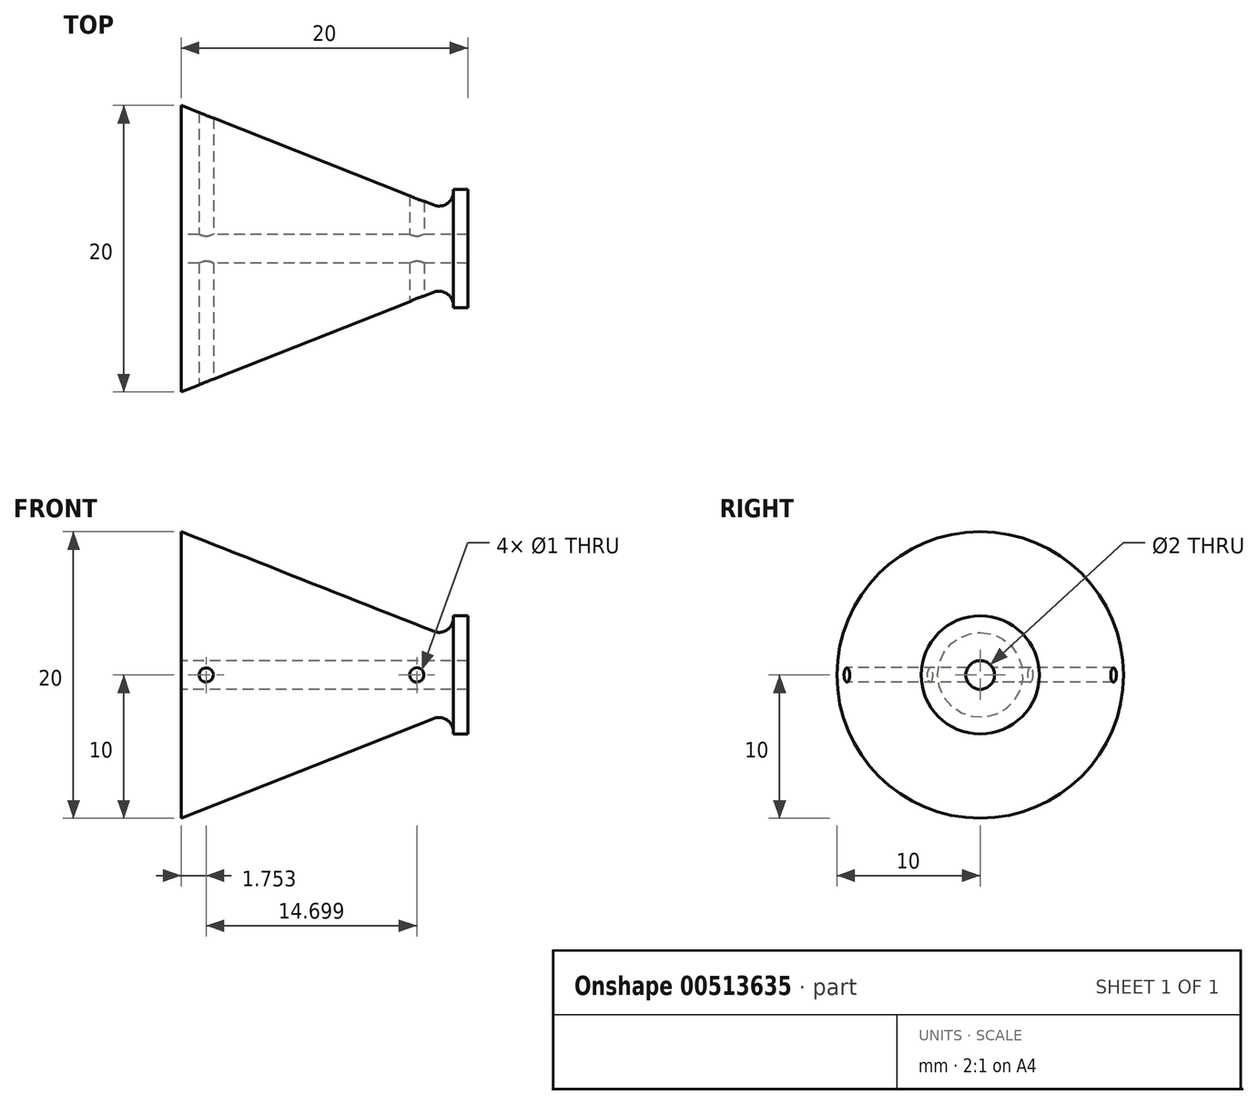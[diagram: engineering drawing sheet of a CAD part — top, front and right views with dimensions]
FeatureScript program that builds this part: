
annotation { "Feature Type Name" : "Feature", "Feature Type Description" : "" }
export const myFeature = defineFeature(function(context is Context, id is Id, definition is map)
    precondition{}
    {
        {
            var Q0;
            Q0=qCreatedBy(makeId("Front.planeOp"),FACE);
            var sketch = newSketch(context, id + "F0", { "sketchPlane" : qUnion([Q0])});
            skLineSegment(sketch, "E0", {"start": v(-20.44, 0) * mm, "end": v(36.79, 0) * mm, "construction": true});
            skLineSegment(sketch, "E1", {"start": v(0, 1) * mm, "end": v(0, 10) * mm});
            skLineSegment(sketch, "E2", {"start": v(0, 10) * mm, "end": v(19, 2.5) * mm});
            skLineSegment(sketch, "E3", {"start": v(19, 2.5) * mm, "end": v(19, 4.12) * mm});
            skLineSegment(sketch, "E4", {"start": v(19, 4.12) * mm, "end": v(20, 4.12) * mm});
            skLineSegment(sketch, "E5", {"start": v(20, 4.12) * mm, "end": v(20, 1) * mm});
            skLineSegment(sketch, "E6", {"start": v(0, 1) * mm, "end": v(20, 1) * mm});
            skSolve(sketch);
        }
        {
            var Q0;
            Q0=makeQuery(id+"F0.imprint","IMPRINT",FACE,{"disambiguationData":[TD([[makeQuery(id+"F0.imprint","IMPRINT",EDGE,{"derivedFrom":sQuery(id+"F0.wireOp",EDGE,"E1")}),-1.0]])]});
            var Q1;
            Q1=sQuery(id+"F0.wireOp",EDGE,"E0");
            revolve(context, id + "F1", {"entities" : qUnion([Q0]), "axis" : qUnion([Q1]), "revolveType" : RevolveType.FULL});
        }
        {
            var Q0;
            Q0=makeQuery(id+"F1.opRevolve","SWEPT_EDGE",EDGE,{"disambiguationData":[OSD([sQuery(id+"F0.wireOp",EDGE,"E2"),sQuery(id+"F0.wireOp",EDGE,"E3")])]});
            fillet(context, id + "F2", {"entities" : qUnion([Q0]), "radius" : 1 * mm, "tangentPropagation" : true, "allowEdgeOverflow" : false});
        }
        {
            var Q0;
            Q0=qCreatedBy(makeId("Front.planeOp"),FACE);
            var sketch = newSketch(context, id + "F3", { "sketchPlane" : qUnion([Q0])});
            skCircle(sketch, "E7", {"center": v(1.75, 0) * mm, "radius": 0.5 * mm});
            skCircle(sketch, "E8", {"center": v(16.45, 0) * mm, "radius": 0.5 * mm});
            skSolve(sketch);
        }
        {
            var Q0;
            Q0 = qSketchRegion(id + "F3", true);
            extrude(context, id + "F4", {"entities" : qUnion([Q0]), "operationType" : NewBodyOperationType.REMOVE, "endBound" : BoundingType.THROUGH_ALL, "oppositeDirection" : true, "depth" : 25 * mm, "offsetDistance" : 25 * mm, "hasSecondDirection" : true, "secondDirectionBound" : SecondDirectionBoundingType.THROUGH_ALL, "secondDirectionOppositeDirection" : false, "secondDirectionDepth" : 25 * mm});
        }
    });
